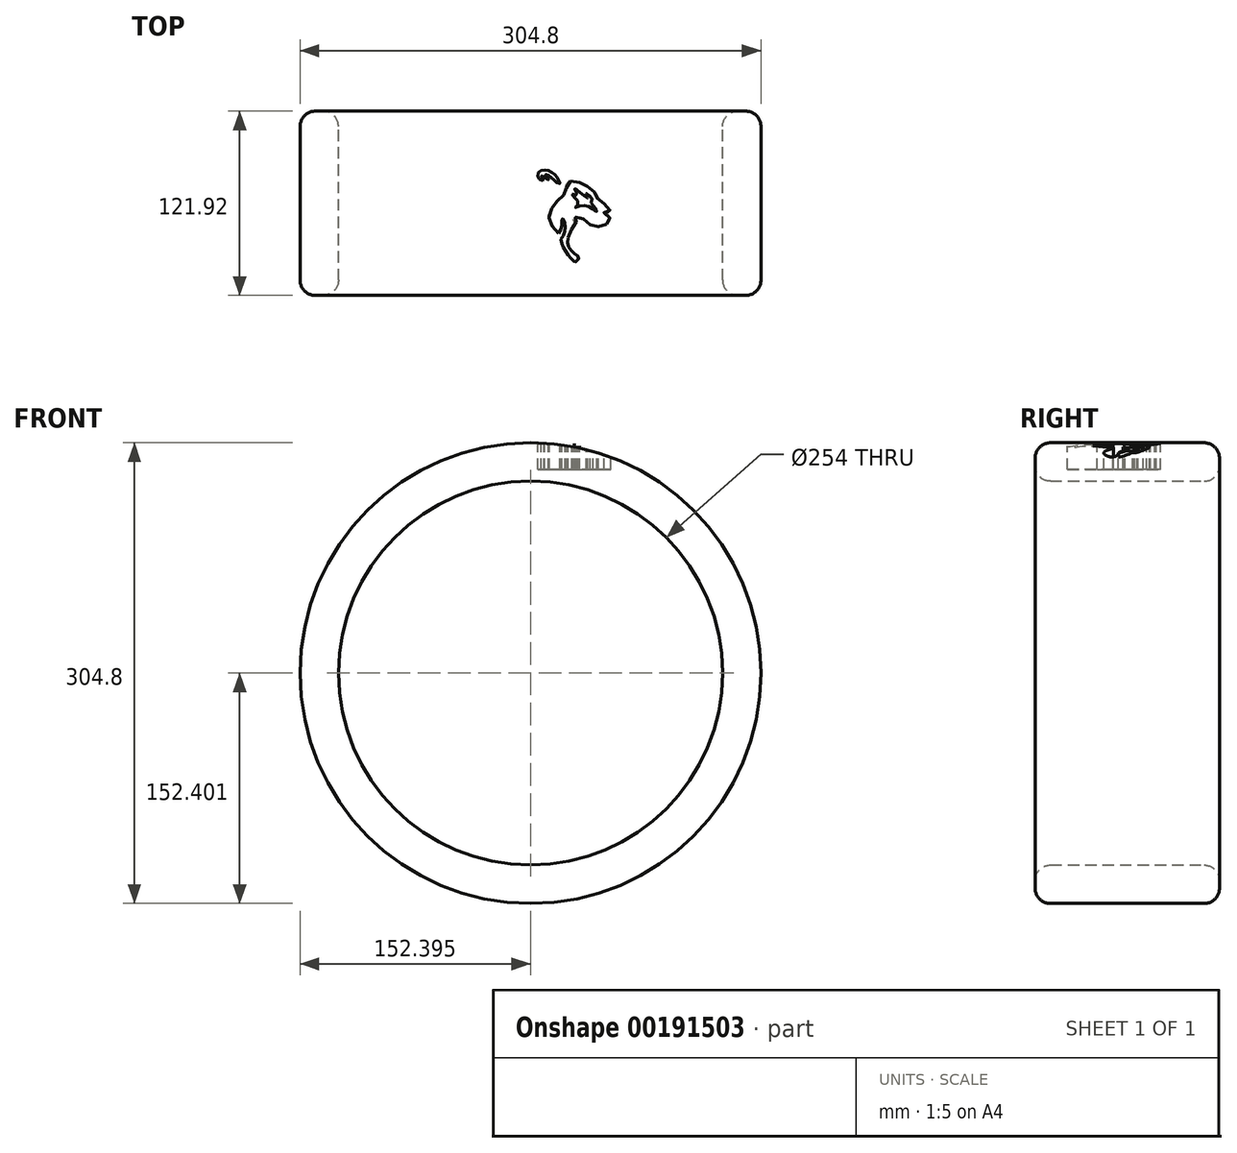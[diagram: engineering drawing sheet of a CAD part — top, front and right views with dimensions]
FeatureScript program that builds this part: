
annotation { "Feature Type Name" : "Feature", "Feature Type Description" : "" }
export const myFeature = defineFeature(function(context is Context, id is Id, definition is map)
    precondition{}
    {
        {
            var Q0;
            Q0=qCreatedBy(makeId("Top.planeOp"),FACE);
            var sketch = newSketch(context, id + "F0", { "sketchPlane" : qUnion([Q0])});
            skFitSpline(sketch, "E0", {"points": [v(-14.87, -19.96) * mm, v(-16.53, -17.13) * mm, v(-18.86, -13.58) * mm, v(-21.78, -9.61) * mm, v(-24.55, -6.73) * mm, v(-29.24, -2.2) * mm, v(-33.32, 1.06) * mm, v(-37.46, 3.8) * mm, v(-40.9, 5.46) * mm, v(-43.35, 6.3) * mm, v(-45.8, 6.8) * mm, v(-46.1, 7) * mm, v(-45.1, 7.59) * mm, v(-39.68, 8.6) * mm, v(-34.05, 9.1) * mm, v(-26.3, 9.07) * mm, v(-20, 8.52) * mm, v(-11.98, 6.95) * mm, v(-2.95, 4.5) * mm, v(7.46, -0.37) * mm, v(7.58, -0.43) * mm, v(5.39, 1.58) * mm, v(1.22, 4.64) * mm, v(-6.3, 8.72) * mm, v(-13.47, 10.97) * mm, v(-20.35, 12.54) * mm, v(-32.07, 13.18) * mm, v(-42.1, 12.72) * mm, v(-42, 12.83) * mm, v(-37.72, 17.5) * mm, v(-31.7, 23.1) * mm, v(-29.15, 25.2) * mm, v(-24.9, 25.08) * mm, v(-20.47, 24.47) * mm, v(-15.32, 23.36) * mm, v(-11.1, 22.1) * mm, v(-6, 20.24) * mm, v(-1.72, 18.52) * mm, v(2.27, 16.6) * mm, v(8.16, 13.3) * mm, v(13.4, 9.63) * mm, v(15.68, 7.8) * mm, v(15.68, 7.82) * mm, v(14.13, 9.77) * mm, v(12.1, 12.08) * mm, v(8.3, 15.63) * mm, v(5.1, 18.14) * mm, v(0.78, 20.85) * mm, v(-6.8, 24.67) * mm, v(-16.6, 27.67) * mm, v(-19.8, 28.49) * mm, v(-23.88, 28.93) * mm, v(-27.84, 29.13) * mm, v(-28.83, 29.25) * mm, v(-28.25, 30.03) * mm, v(-24.92, 31.85) * mm, v(-18.83, 34.06) * mm, v(-13.56, 35.28) * mm, v(-9.07, 35.69) * mm, v(-3.03, 35.3) * mm, v(3.32, 33.44) * mm, v(8.22, 31.43) * mm, v(14.57, 27.73) * mm, v(19.8, 23.97) * mm, v(25.5, 18.58) * mm, v(29.06, 15.28) * mm, v(29.06, 15.31) * mm, v(27.98, 16.94) * mm, v(25.97, 19.45) * mm, v(22.94, 23.1) * mm, v(19.59, 26.07) * mm, v(16.79, 28.66) * mm, v(12.12, 32.04) * mm, v(7.7, 34.26) * mm, v(0, 37.44) * mm, v(-4.46, 38.57) * mm, v(-9.33, 39.6) * mm, v(-9.3, 39.74) * mm, v(-7.35, 40.32) * mm, v(1.8, 40.56) * mm, v(8.65, 39.94) * mm, v(15.65, 38.31) * mm, v(20.75, 36.65) * mm, v(27.72, 32.86) * mm, v(27.72, 32.89) * mm, v(27.46, 36.7) * mm, v(27.52, 36.77) * mm, v(31.83, 34.93) * mm, v(36.67, 32.57) * mm, v(42.64, 28.75) * mm, v(48.48, 24.06) * mm, v(52.7, 18.98) * mm, v(54.89, 13.8) * mm, v(55.33, 9.69) * mm, v(55.18, 7.18) * mm, v(55.27, 7.1) * mm, v(57.42, 4.85) * mm, v(60.51, 1.35) * mm, v(61.91, -0.72) * mm, v(61.88, -0.8) * mm, v(60.78, -1.71) * mm, v(60.9, -1.8) * mm, v(63.2, -4.3) * mm, v(66.14, -7.78) * mm, v(67.85, -11.11) * mm, v(67.85, -13.12) * mm, v(67.46, -14.96) * mm, v(65.54, -18.66) * mm, v(63.46, -20.9) * mm, v(62.06, -22.18) * mm, v(62.03, -22.43) * mm, v(60.9, -24.65) * mm, v(58.62, -26.9) * mm, v(55.24, -28.88) * mm, v(52.93, -29.11) * mm, v(52.9, -28.97) * mm, v(54.07, -26.96) * mm, v(53.95, -27.07) * mm, v(52.2, -28.1) * mm, v(50.31, -28.74) * mm, v(46.46, -28.82) * mm, v(46.5, -28.65) * mm, v(49.67, -22.96) * mm, v(49.32, -22.67) * mm, v(48.18, -21.97) * mm, v(47.13, -20.96) * mm, v(47.05, -20.96) * mm, v(46.7, -21.42) * mm, v(45.15, -23.14) * mm, v(44.22, -23.85) * mm, v(44.1, -24.19) * mm, v(44.19, -29.7) * mm, v(44.22, -29.7) * mm, v(44.92, -28.76) * mm, v(44.95, -28.8) * mm, v(45.44, -29.35) * mm, v(45.8, -30.37) * mm, v(45.9, -32.23) * mm, v(46, -32.23) * mm, v(47.48, -30.69) * mm, v(47.54, -30.69) * mm, v(47.98, -31.21) * mm, v(48.42, -32.87) * mm, v(48.68, -36.43) * mm, v(47.54, -38.62) * mm, v(47.37, -39.43) * mm, v(46.46, -42.26) * mm, v(44.66, -45.2) * mm, v(41.97, -47.1) * mm, v(38.65, -48.03) * mm, v(34.77, -47.92) * mm, v(34.74, -47.86) * mm, v(36.17, -45.32) * mm, v(36.17, -45.26) * mm, v(34.07, -43.66) * mm, v(30.98, -41.07) * mm, v(29.12, -39.32) * mm, v(27.14, -36.66) * mm, v(26.2, -34.83) * mm, v(25.45, -32.87) * mm, v(24.9, -30.05) * mm, v(24.75, -28.85) * mm, v(24.66, -28.8) * mm, v(23.29, -27.54) * mm, v(21.74, -25.69) * mm, v(20.52, -23.85) * mm, v(18.68, -20.22) * mm, v(17.37, -17.45) * mm, v(16.55, -14.63) * mm, v(15.91, -12.2) * mm, v(15.77, -9.76) * mm, v(15.68, -9.76) * mm, v(15.36, -12.64) * mm, v(15.27, -16.23) * mm, v(16.12, -20.1) * mm, v(17.46, -23.43) * mm, v(19.24, -26.14) * mm, v(22.06, -29.32) * mm, v(22.27, -29.52) * mm, v(22.3, -30.95) * mm, v(22.73, -33.22) * mm, v(23.96, -35.85) * mm, v(23.93, -36) * mm, v(22.82, -36.98) * mm, v(20.93, -39.55) * mm, v(19.88, -41.24) * mm, v(19.24, -43.28) * mm, v(19.1, -43.4) * mm, v(18.57, -43.08) * mm, v(17.87, -42.17) * mm, v(17.08, -41.15) * mm, v(16.06, -39.6) * mm, v(15.65, -38.9) * mm, v(15.62, -38.94) * mm, v(14.51, -40.3) * mm, v(13.32, -42.03) * mm, v(11.95, -44.27) * mm, v(11.07, -46.34) * mm, v(10.35, -48.41) * mm, v(9.62, -50.86) * mm, v(9.35, -52.58) * mm, v(9.3, -52.58) * mm, v(7.52, -52.23) * mm, v(6.06, -51.74) * mm, v(4.14, -50.95) * mm, v(2.62, -50.28) * mm, v(0.46, -49.2) * mm, v(-0.88, -48.32) * mm, v(-2.69, -47.13) * mm, v(-4.06, -46.14) * mm, v(-5.37, -45) * mm, v(-6.5, -43.86) * mm, v(-7.09, -43.08) * mm, v(-7.35, -41.82) * mm, v(-7.58, -39.96) * mm, v(-8.43, -37.07) * mm, v(-9.27, -34.13) * mm, v(-10.79, -29.55) * mm, v(-12.22, -25.9) * mm, v(-14.26, -21.53) * mm, v(-14.87, -19.96) * mm]});
            skFitSpline(sketch, "E1", {"points": [v(20.64, 14.12) * mm, v(21.76, 13.88) * mm, v(23.17, 13.2) * mm, v(24.26, 12.5) * mm, v(25.27, 11.74) * mm, v(26.44, 10.52) * mm, v(27.07, 9.84) * mm, v(27.64, 9.1) * mm, v(27.7, 9.06) * mm, v(30.4, 7.75) * mm, v(30.5, 7.73) * mm, v(30.46, 7.97) * mm, v(30.13, 9) * mm, v(29.51, 10.69) * mm, v(28.86, 12.03) * mm, v(27.76, 13.35) * mm, v(26.8, 14.2) * mm, v(25.54, 15.12) * mm, v(24.24, 15.9) * mm, v(23, 16.5) * mm, v(21.47, 16.84) * mm, v(19.08, 16.75) * mm, v(17.8, 16.44) * mm, v(16.92, 15.9) * mm, v(16.42, 15.22) * mm, v(16.11, 14.43) * mm, v(15.98, 12.98) * mm, v(16.3, 11.89) * mm, v(16.76, 11.13) * mm, v(17.4, 10.34) * mm, v(17.5, 10.21) * mm, v(20.2, 10.12) * mm, v(20.2, 10.16) * mm, v(20, 10.47) * mm, v(19.46, 11.3) * mm, v(18.95, 11.9) * mm, v(18.42, 12.67) * mm, v(18.18, 13.08) * mm, v(18.18, 13.1) * mm, v(18.77, 12.97) * mm, v(20.42, 12.07) * mm, v(21.6, 11.22) * mm, v(23.34, 10) * mm, v(23.4, 10.01) * mm, v(23.45, 10.34) * mm, v(22.77, 11.31) * mm, v(21.82, 12.43) * mm, v(21.06, 13.19) * mm, v(20.47, 13.8) * mm, v(20.36, 14.07) * mm, v(20.64, 14.12) * mm]});
            skFitSpline(sketch, "E2", {"points": [v(29.5, -24.96) * mm, v(28.58, -24.35) * mm, v(27.6, -23.28) * mm, v(26.55, -21.99) * mm, v(25.54, -20.52) * mm, v(24.7, -18.86) * mm, v(23.88, -16.81) * mm, v(23.47, -15.09) * mm, v(22.99, -12.75) * mm, v(23.1, -12.53) * mm, v(23.95, -10.91) * mm, v(24.86, -9.04) * mm, v(25.75, -7.35) * mm, v(26.7, -5.8) * mm, v(27.88, -4.41) * mm, v(29.43, -2.66) * mm, v(31.27, -0.9) * mm, v(33.27, 0.81) * mm, v(35.98, 3.21) * mm, v(35.98, 3.28) * mm, v(35.63, 3.76) * mm, v(35.07, 4.35) * mm, v(34.8, 4.96) * mm, v(34.63, 5.81) * mm, v(34.7, 7.06) * mm, v(34.93, 7.73) * mm, v(35.94, 8.78) * mm, v(36.81, 9.33) * mm, v(38.01, 9.61) * mm, v(39.35, 9.66) * mm, v(40.85, 9.42) * mm, v(42.3, 9.1) * mm, v(43.98, 8.55) * mm, v(45.84, 7.68) * mm, v(47.83, 6.54) * mm, v(49.9, 5.2) * mm, v(51.6, 3.98) * mm, v(52.98, 2.8) * mm, v(53.93, 1.93) * mm, v(55, 0.77) * mm, v(56.05, -0.54) * mm, v(56.03, -0.56) * mm, v(54.91, -1.2) * mm, v(56.03, -2.2) * mm, v(57.65, -3.42) * mm, v(59.34, -4.88) * mm, v(61.47, -7.1) * mm, v(63.04, -8.9) * mm, v(64.22, -10.48) * mm, v(64.2, -10.5) * mm, v(59.74, -11.02) * mm, v(59.72, -11.02) * mm, v(59.74, -11.42) * mm, v(59.9, -11.48) * mm, v(60.57, -11.75) * mm, v(62.04, -12.36) * mm, v(62.65, -12.6) * mm, v(62.67, -12.62) * mm, v(62.71, -13.34) * mm, v(62.89, -13.71) * mm, v(63.48, -14.6) * mm, v(64.22, -15.52) * mm, v(64.24, -15.74) * mm, v(63.94, -16.3) * mm, v(63.43, -17) * mm, v(62.73, -17.9) * mm, v(61.93, -18.67) * mm, v(60.8, -19.43) * mm, v(59.6, -19.98) * mm, v(58.43, -20.37) * mm, v(57.17, -20.61) * mm, v(54.26, -20.46) * mm, v(52.54, -20.04) * mm, v(51.49, -19.56) * mm, v(49.87, -18.62) * mm, v(48.5, -17.51) * mm, v(47.3, -16.44) * mm, v(45.88, -15.17) * mm, v(44.76, -14.52) * mm, v(44.04, -14.3) * mm, v(41.64, -14.17) * mm, v(40.04, -14.54) * mm, v(39.04, -15.41) * mm, v(39.08, -15.44) * mm, v(41.8, -16.57) * mm, v(41.82, -16.65) * mm, v(40.93, -18) * mm, v(39.82, -19.8) * mm, v(38.1, -22.76) * mm, v(36.88, -24.94) * mm, v(36.12, -27.16) * mm, v(35.87, -29.14) * mm, v(35.87, -32.06) * mm, v(36.24, -33.32) * mm, v(37, -35.08) * mm, v(38.26, -36.67) * mm, v(39.49, -37.84) * mm, v(41.2, -39.1) * mm, v(42.76, -39.92) * mm, v(43.55, -40.27) * mm, v(43.61, -40.33) * mm, v(43.34, -41.19) * mm, v(42.78, -42.37) * mm, v(41.7, -43.5) * mm, v(39.96, -44.59) * mm, v(39.96, -44.57) * mm, v(40.25, -43.87) * mm, v(40.3, -43.77) * mm, v(39.86, -43.27) * mm, v(38.83, -42.37) * mm, v(37.58, -41.13) * mm, v(36.04, -39.4) * mm, v(34.86, -37.76) * mm, v(33.78, -36.12) * mm, v(32.58, -33.71) * mm, v(31.7, -31.43) * mm, v(31.06, -29.18) * mm, v(31.06, -29.1) * mm, v(31.73, -28.48) * mm, v(32.62, -26.8) * mm, v(33.3, -25.15) * mm, v(33.67, -23.64) * mm, v(33.9, -21.67) * mm, v(33.87, -19.43) * mm, v(33.67, -17.84) * mm, v(33.1, -16.36) * mm, v(31.92, -14.6) * mm, v(31.92, -14.67) * mm, v(31.88, -16.13) * mm, v(31.92, -18.77) * mm, v(31.78, -19.78) * mm, v(31.5, -21.26) * mm, v(31.1, -22.48) * mm, v(30.62, -23.69) * mm, v(29.88, -24.82) * mm, v(29.5, -24.96) * mm]});
            skFitSpline(sketch, "E3", {"points": [v(38.42, 1.18) * mm, v(39.29, 1.15) * mm, v(40.25, 0.8) * mm, v(41.21, 0.31) * mm, v(41.88, -0.27) * mm, v(42, 1.04) * mm, v(41.85, 1.4) * mm, v(41.47, 2.15) * mm, v(40.8, 3.44) * mm, v(40.14, 5.4) * mm, v(40.27, 5.48) * mm, v(40.92, 4.71) * mm, v(42.09, 3.55) * mm, v(43.78, 2.2) * mm, v(45.64, 0.72) * mm, v(48.76, -1.62) * mm, v(48.65, -0.59) * mm, v(48.35, 0.81) * mm, v(48.14, 1.88) * mm, v(48.27, 1.95) * mm, v(49.02, 1.25) * mm, v(50, 0.31) * mm, v(51.08, -1) * mm, v(52.33, -3.64) * mm, v(51.05, -4.61) * mm, v(50.7, -5.43) * mm, v(52.05, -6.37) * mm, v(54, -8.43) * mm, v(55.42, -10.4) * mm, v(55.36, -10.94) * mm, v(54.7, -10.56) * mm, v(53.66, -9.71) * mm, v(52.53, -8.9) * mm, v(51.42, -8.2) * mm, v(50.02, -7.38) * mm, v(48.75, -6.77) * mm, v(48.26, -6.65) * mm, v(47.4, -6.6) * mm, v(46.02, -6.65) * mm, v(44.24, -6.89) * mm, v(42.3, -7.38) * mm, v(40.41, -7.78) * mm, v(40.83, -6.76) * mm, v(42.29, -6.14) * mm, v(42.68, -5.5) * mm, v(42.64, -4.48) * mm, v(42.09, -3.21) * mm, v(40.68, -1.57) * mm, v(39.33, -0.38) * mm, v(38.62, 0.45) * mm, v(38.42, 0.86) * mm, v(38.42, 1.18) * mm]});
            skFitSpline(sketch, "E4.0", {"points": [v(-37, 28.67) * mm, v(-36.89, 28.92) * mm, v(-36.76, 29.16) * mm, v(-36.57, 29.48) * mm, v(-36.3, 29.86) * mm, v(-35.9, 30.24) * mm, v(-35.52, 30.53) * mm, v(-35.17, 30.74) * mm, v(-34.88, 30.9) * mm, v(-34.64, 31) * mm, v(-34.44, 31.1) * mm, v(-34.26, 31.2) * mm, v(-34.04, 31.32) * mm, v(-33.79, 31.47) * mm, v(-33.42, 31.7) * mm, v(-32.9, 32.04) * mm, v(-32.2, 32.49) * mm, v(-31.46, 32.97) * mm, v(-30.66, 33.45) * mm, v(-29.97, 33.85) * mm, v(-29.4, 34.16) * mm, v(-28.83, 34.46) * mm, v(-28.13, 34.78) * mm, v(-27.05, 35.24) * mm, v(-26.05, 35.64) * mm, v(-25.09, 36.06) * mm, v(-24.38, 36.4) * mm, v(-23.78, 36.72) * mm, v(-23.3, 37.01) * mm, v(-22.8, 37.33) * mm, v(-22.15, 37.79) * mm, v(-21.3, 38.43) * mm, v(-20.43, 39.12) * mm, v(-19.53, 39.85) * mm, v(-18.62, 40.6) * mm, v(-17.7, 41.32) * mm, v(-16.79, 42.02) * mm, v(-16.02, 42.56) * mm, v(-15.4, 42.95) * mm, v(-14.93, 43.23) * mm, v(-14.45, 43.48) * mm, v(-13.78, 43.79) * mm, v(-12.97, 44.06) * mm, v(-12.06, 44.25) * mm, v(-11.23, 44.33) * mm, v(-10.64, 44.35) * mm, v(-10.23, 44.35) * mm, v(-9.95, 44.35) * mm, v(-9.7, 44.36) * mm, v(-9.4, 44.37) * mm, v(-9, 44.4) * mm, v(-8.49, 44.45) * mm, v(-7.94, 44.52) * mm, v(-7.35, 44.6) * mm, v(-6.82, 44.66) * mm, v(-6.38, 44.7) * mm, v(-5.72, 44.77) * mm, v(-4.7, 44.85) * mm, v(-3.3, 44.93) * mm, v(-1.81, 45) * mm, v(-0.24, 45.06) * mm, v(1.39, 45.1) * mm, v(2.74, 45.1) * mm, v(3.8, 45.08) * mm, v(4.82, 45.04) * mm, v(6.04, 44.95) * mm, v(7.23, 44.85) * mm, v(8.19, 44.76) * mm, v(9.17, 44.67) * mm, v(10.2, 44.57) * mm, v(11.21, 44.46) * mm, v(11.95, 44.36) * mm, v(12.54, 44.27) * mm, v(13, 44.18) * mm, v(13.34, 44.1) * mm, v(13.65, 44.03) * mm, v(14.02, 43.93) * mm, v(14.41, 43.81) * mm, v(14.8, 43.7) * mm, v(15.15, 43.62) * mm, v(15.47, 43.57) * mm, v(15.84, 43.52) * mm, v(16.44, 43.45) * mm, v(17.33, 43.4) * mm, v(18.33, 43.35) * mm, v(19.41, 43.3) * mm, v(20.92, 43.25) * mm, v(22.47, 43.18) * mm, v(23.95, 43.07) * mm, v(25, 42.96) * mm, v(26, 42.82) * mm, v(26.89, 42.63) * mm, v(27.7, 42.41) * mm, v(28.43, 42.17) * mm, v(29.1, 41.91) * mm, v(29.64, 41.7) * mm, v(30.05, 41.52) * mm, v(30.46, 41.35) * mm, v(31, 41.13) * mm, v(31.7, 40.85) * mm, v(32.67, 40.45) * mm, v(33.69, 40.03) * mm, v(34.7, 39.6) * mm, v(35.45, 39.26) * mm, v(36.17, 38.92) * mm, v(37.09, 38.47) * mm, v(38.15, 37.91) * mm, v(39.13, 37.39) * mm, v(39.87, 36.99) * mm, v(40.6, 36.6) * mm, v(41.53, 36.1) * mm, v(42.66, 35.5) * mm, v(43.81, 34.85) * mm, v(44.77, 34.25) * mm, v(45.54, 33.75) * mm, v(46.1, 33.36) * mm, v(46.66, 32.94) * mm, v(47.18, 32.54) * mm, v(47.67, 32.14) * mm, v(48.15, 31.75) * mm, v(48.62, 31.37) * mm, v(49, 31.07) * mm, v(49.31, 30.84) * mm, v(49.64, 30.6) * mm, v(50.06, 30.29) * mm, v(50.6, 29.88) * mm, v(51.17, 29.45) * mm, v(51.65, 29.05) * mm, v(52.04, 28.7) * mm, v(52.33, 28.42) * mm, v(52.61, 28.13) * mm, v(52.97, 27.75) * mm, v(53.38, 27.27) * mm, v(53.83, 26.7) * mm, v(54.25, 26.15) * mm, v(54.63, 25.65) * mm, v(54.93, 25.26) * mm, v(55.15, 24.99) * mm, v(55.38, 24.71) * mm, v(55.68, 24.37) * mm, v(56.05, 23.94) * mm, v(56.44, 23.49) * mm, v(56.83, 23) * mm, v(57.23, 22.46) * mm, v(57.6, 21.9) * mm, v(58.06, 21.15) * mm, v(58.57, 20.18) * mm, v(59.13, 18.98) * mm, v(59.62, 17.76) * mm, v(59.98, 16.77) * mm, v(60.23, 16.02) * mm, v(60.45, 15.29) * mm, v(60.7, 14.37) * mm, v(61.06, 13.09) * mm, v(61.53, 11.43) * mm, v(62, 9.95) * mm, v(62.37, 8.83) * mm, v(62.65, 8.05) * mm, v(62.88, 7.5) * mm, v(63.05, 7.13) * mm, v(63.16, 6.9) * mm, v(63.26, 6.73) * mm, v(63.38, 6.53) * mm, v(63.52, 6.34) * mm, v(63.72, 6.1) * mm, v(63.96, 5.84) * mm, v(64.2, 5.58) * mm, v(64.46, 5.28) * mm, v(64.79, 4.88) * mm, v(65.19, 4.37) * mm, v(65.59, 3.84) * mm, v(65.99, 3.28) * mm, v(66.39, 2.7) * mm, v(66.78, 2.12) * mm, v(67.16, 1.55) * mm, v(67.51, 1) * mm, v(67.84, 0.49) * mm, v(68.11, 0.03) * mm, v(68.34, -0.36) * mm, v(68.51, -0.67) * mm, v(68.65, -0.92) * mm, v(68.8, -1.2) * mm, v(69.07, -1.66) * mm, v(69.4, -2.22) * mm, v(69.79, -2.85) * mm, v(70.2, -3.51) * mm, v(70.61, -4.17) * mm, v(71.01, -4.79) * mm, v(71.37, -5.32) * mm, v(71.68, -5.77) * mm, v(71.97, -6.16) * mm, v(72.24, -6.53) * mm, v(72.54, -6.9) * mm, v(72.85, -7.3) * mm, v(73.24, -7.8) * mm, v(73.65, -8.36) * mm, v(74.06, -9.02) * mm, v(74.38, -9.66) * mm, v(74.6, -10.22) * mm, v(74.72, -10.6) * mm, v(74.8, -10.92) * mm, v(74.87, -11.22) * mm, v(74.92, -11.6) * mm, v(74.96, -12.03) * mm, v(74.99, -12.59) * mm, v(74.97, -13.24) * mm, v(74.9, -13.92) * mm, v(74.84, -14.4) * mm, v(74.79, -14.72) * mm, v(74.74, -15.02) * mm, v(74.67, -15.4) * mm, v(74.58, -15.8) * mm, v(74.48, -16.12) * mm, v(74.36, -16.45) * mm, v(74.21, -16.83) * mm, v(74.03, -17.26) * mm, v(73.87, -17.61) * mm, v(73.76, -17.88) * mm, v(73.64, -18.15) * mm, v(73.49, -18.53) * mm, v(73.27, -19.04) * mm, v(73.06, -19.5) * mm, v(72.85, -19.88) * mm, v(72.68, -20.17) * mm, v(72.48, -20.47) * mm, v(72.28, -20.73) * mm, v(72.09, -20.97) * mm, v(71.85, -21.24) * mm, v(71.63, -21.47) * mm, v(71.47, -21.65) * mm, v(71.38, -21.75) * mm, v(71.33, -21.81) * mm, v(71.27, -21.88) * mm, v(71.2, -21.98) * mm, v(71.09, -22.1) * mm, v(70.94, -22.3) * mm, v(70.76, -22.54) * mm, v(70.54, -22.8) * mm, v(70.36, -23.02) * mm, v(70.17, -23.22) * mm, v(69.93, -23.47) * mm, v(69.62, -23.76) * mm, v(69.34, -24.02) * mm, v(69.13, -24.22) * mm, v(68.99, -24.35) * mm, v(68.84, -24.5) * mm, v(68.64, -24.68) * mm, v(68.37, -24.94) * mm, v(68.06, -25.21) * mm, v(67.8, -25.44) * mm, v(67.5, -25.67) * mm, v(67.18, -25.9) * mm, v(66.91, -26.11) * mm, v(66.75, -26.24) * mm, v(66.66, -26.32) * mm, v(66.6, -26.37) * mm, v(66.6, -26.38) * mm, v(66.59, -26.4) * mm, v(66.56, -26.44) * mm, v(66.5, -26.52) * mm, v(66.43, -26.64) * mm, v(66.33, -26.82) * mm, v(66.22, -27) * mm, v(66.1, -27.15) * mm, v(66, -27.3) * mm, v(65.88, -27.49) * mm, v(65.72, -27.7) * mm, v(65.52, -27.95) * mm, v(65.28, -28.26) * mm, v(65.06, -28.54) * mm, v(64.92, -28.73) * mm, v(64.81, -28.9) * mm, v(64.7, -29.07) * mm, v(64.52, -29.32) * mm, v(64.27, -29.68) * mm, v(63.97, -30.05) * mm, v(63.74, -30.3) * mm, v(63.58, -30.47) * mm, v(63.37, -30.67) * mm, v(63.12, -30.89) * mm, v(62.78, -31.15) * mm, v(62.38, -31.44) * mm, v(61.98, -31.7) * mm, v(61.68, -31.89) * mm, v(61.47, -32.02) * mm, v(61.25, -32.16) * mm, v(60.94, -32.35) * mm, v(60.52, -32.6) * mm, v(60.06, -32.85) * mm, v(59.67, -33.04) * mm, v(59.35, -33.18) * mm, v(59.08, -33.28) * mm, v(58.85, -33.36) * mm, v(58.63, -33.43) * mm, v(58.38, -33.5) * mm, v(58.02, -33.6) * mm, v(57.65, -33.69) * mm, v(57.3, -33.79) * mm, v(57.06, -33.89) * mm, v(56.87, -33.99) * mm, v(56.7, -34.08) * mm, v(56.52, -34.21) * mm, v(56.24, -34.41) * mm, v(55.88, -34.72) * mm, v(55.45, -35.15) * mm, v(55.06, -35.61) * mm, v(54.74, -36.06) * mm, v(54.55, -36.4) * mm, v(54.46, -36.62) * mm, v(54.38, -36.84) * mm, v(54.3, -37.13) * mm, v(54.24, -37.55) * mm, v(54.2, -37.99) * mm, v(54.16, -38.39) * mm, v(54.13, -38.71) * mm, v(54.1, -39.01) * mm, v(54.05, -39.26) * mm, v(54, -39.52) * mm, v(53.93, -39.84) * mm, v(53.8, -40.32) * mm, v(53.62, -40.89) * mm, v(53.38, -41.51) * mm, v(53.14, -42.1) * mm, v(52.96, -42.55) * mm, v(52.82, -42.9) * mm, v(52.69, -43.27) * mm, v(52.51, -43.77) * mm, v(52.28, -44.43) * mm, v(52.02, -45.13) * mm, v(51.7, -45.87) * mm, v(51.38, -46.5) * mm, v(51.08, -47.02) * mm, v(50.75, -47.53) * mm, v(50.3, -48.12) * mm, v(49.7, -48.78) * mm, v(48.85, -49.58) * mm, v(47.72, -50.46) * mm, v(46.3, -51.35) * mm, v(44.83, -52.1) * mm, v(43.35, -52.7) * mm, v(41.9, -53.15) * mm, v(40.51, -53.43) * mm, v(39.39, -53.55) * mm, v(38.61, -53.58) * mm, v(38.17, -53.59) * mm, v(37.71, -53.6) * mm, v(37.13, -53.58) * mm, v(36.41, -53.53) * mm, v(35.8, -53.45) * mm, v(35.3, -53.36) * mm, v(34.93, -53.27) * mm, v(34.62, -53.18) * mm, v(34.36, -53.1) * mm, v(34.13, -53) * mm, v(33.87, -52.9) * mm, v(33.52, -52.74) * mm, v(33.22, -52.6) * mm, v(32.99, -52.53) * mm, v(32.78, -52.5) * mm, v(32.53, -52.48) * mm, v(32.3, -52.48) * mm, v(31.98, -52.5) * mm, v(31.58, -52.56) * mm, v(31.1, -52.65) * mm, v(30.4, -52.8) * mm, v(29.38, -53.06) * mm, v(27.54, -53.58) * mm, v(24.94, -54.4) * mm, v(21.58, -55.49) * mm, v(18.76, -56.35) * mm, v(16.6, -56.93) * mm, v(15.03, -57.29) * mm, v(13.78, -57.52) * mm, v(12.83, -57.64) * mm, v(12.13, -57.7) * mm, v(11.45, -57.72) * mm, v(10.6, -57.69) * mm, v(9.63, -57.57) * mm, v(8.63, -57.32) * mm, v(7.95, -57.08) * mm, v(7.5, -56.88) * mm, v(7.2, -56.75) * mm, v(6.97, -56.63) * mm, v(6.82, -56.56) * mm, v(6.75, -56.53) * mm, v(6.72, -56.51) * mm, v(6.7, -56.5) * mm, v(6.69, -56.5) * mm, v(6.67, -56.5) * mm, v(6.57, -56.47) * mm, v(6.33, -56.41) * mm, v(6.03, -56.32) * mm, v(5.83, -56.26) * mm, v(5.64, -56.2) * mm, v(5.38, -56.1) * mm, v(4.96, -55.95) * mm, v(4.4, -55.74) * mm, v(3.72, -55.47) * mm, v(3.18, -55.27) * mm, v(2.78, -55.12) * mm, v(2.52, -55.03) * mm, v(2.33, -54.97) * mm, v(2.21, -54.94) * mm, v(2.11, -54.91) * mm, v(2, -54.88) * mm, v(1.87, -54.86) * mm, v(1.7, -54.82) * mm, v(1.49, -54.78) * mm, v(1.22, -54.72) * mm, v(0.95, -54.64) * mm, v(0.72, -54.55) * mm, v(0.5, -54.46) * mm, v(0.27, -54.34) * mm, v(0.01, -54.2) * mm, v(-0.3, -54.01) * mm, v(-0.65, -53.79) * mm, v(-0.96, -53.59) * mm, v(-1.17, -53.45) * mm, v(-1.4, -53.32) * mm, v(-1.71, -53.14) * mm, v(-2.12, -52.91) * mm, v(-2.56, -52.66) * mm, v(-3.18, -52.28) * mm, v(-3.75, -51.9) * mm, v(-4.2, -51.58) * mm, v(-4.46, -51.41) * mm, v(-4.64, -51.3) * mm, v(-4.82, -51.17) * mm, v(-5.07, -51) * mm, v(-5.54, -50.69) * mm, v(-6.16, -50.24) * mm, v(-6.85, -49.67) * mm, v(-7.36, -49.21) * mm, v(-7.85, -48.74) * mm, v(-8.32, -48.28) * mm, v(-8.68, -47.9) * mm, v(-8.93, -47.63) * mm, v(-9.1, -47.43) * mm, v(-9.29, -47.22) * mm, v(-9.53, -46.92) * mm, v(-9.83, -46.47) * mm, v(-10.07, -45.96) * mm, v(-10.22, -45.55) * mm, v(-10.35, -45.16) * mm, v(-10.48, -44.67) * mm, v(-10.62, -44.07) * mm, v(-10.75, -43.45) * mm, v(-10.89, -42.83) * mm, v(-11.02, -42.23) * mm, v(-11.22, -41.42) * mm, v(-11.5, -40.38) * mm, v(-11.79, -39.32) * mm, v(-12.03, -38.45) * mm, v(-12.27, -37.6) * mm, v(-12.58, -36.54) * mm, v(-12.97, -35.3) * mm, v(-13.42, -34.11) * mm, v(-13.88, -33.06) * mm, v(-14.24, -32.23) * mm, v(-14.5, -31.62) * mm, v(-14.76, -31.02) * mm, v(-15.06, -30.24) * mm, v(-15.28, -29.59) * mm, v(-15.48, -29) * mm, v(-15.6, -28.64) * mm, v(-15.72, -28.33) * mm, v(-15.85, -28) * mm, v(-16.04, -27.54) * mm, v(-16.3, -26.96) * mm, v(-16.56, -26.36) * mm, v(-16.83, -25.77) * mm, v(-17.1, -25.18) * mm, v(-17.36, -24.64) * mm, v(-17.7, -23.96) * mm, v(-18.1, -23.18) * mm, v(-18.62, -22.23) * mm, v(-19.27, -21.16) * mm, v(-20.03, -20) * mm, v(-20.71, -18.96) * mm, v(-21.28, -18.1) * mm, v(-21.85, -17.25) * mm, v(-22.42, -16.4) * mm, v(-22.98, -15.6) * mm, v(-23.4, -15.03) * mm, v(-23.8, -14.5) * mm, v(-24.31, -13.84) * mm, v(-24.96, -13.07) * mm, v(-25.6, -12.34) * mm, v(-26.06, -11.82) * mm, v(-26.33, -11.5) * mm, v(-26.72, -11.06) * mm, v(-27.29, -10.4) * mm, v(-27.97, -9.64) * mm, v(-28.58, -9) * mm, v(-29.1, -8.5) * mm, v(-29.67, -7.95) * mm, v(-30.47, -7.2) * mm, v(-31.3, -6.46) * mm, v(-32.1, -5.75) * mm, v(-32.65, -5.26) * mm, v(-33.17, -4.8) * mm, v(-33.61, -4.42) * mm, v(-34.01, -4.08) * mm, v(-34.38, -3.78) * mm, v(-34.76, -3.5) * mm, v(-35.18, -3.2) * mm, v(-35.68, -2.89) * mm, v(-36.44, -2.43) * mm, v(-37.54, -1.81) * mm, v(-38.93, -1.06) * mm, v(-40.3, -0.33) * mm, v(-41.29, 0.18) * mm, v(-42, 0.52) * mm, v(-42.5, 0.74) * mm, v(-42.98, 0.92) * mm, v(-43.41, 1.05) * mm, v(-43.93, 1.18) * mm, v(-44.52, 1.32) * mm, v(-45.19, 1.48) * mm, v(-45.93, 1.7) * mm, v(-46.73, 1.99) * mm, v(-47.58, 2.38) * mm, v(-48.41, 2.85) * mm, v(-49.23, 3.41) * mm, v(-49.87, 3.97) * mm, v(-50.34, 4.51) * mm, v(-50.68, 4.98) * mm, v(-50.97, 5.52) * mm, v(-51.16, 6.07) * mm, v(-51.24, 6.57) * mm, v(-51.26, 6.97) * mm, v(-51.24, 7.35) * mm, v(-51.15, 7.84) * mm, v(-50.96, 8.38) * mm, v(-50.68, 8.9) * mm, v(-50.37, 9.34) * mm, v(-49.95, 9.83) * mm, v(-49.42, 10.34) * mm, v(-48.83, 10.86) * mm, v(-48.4, 11.23) * mm, v(-48.13, 11.49) * mm, v(-47.93, 11.68) * mm, v(-47.74, 11.88) * mm, v(-47.5, 12.16) * mm, v(-47.2, 12.51) * mm, v(-46.83, 12.97) * mm, v(-46.45, 13.47) * mm, v(-46.03, 14) * mm, v(-45.43, 14.77) * mm, v(-44.76, 15.54) * mm, v(-44.04, 16.32) * mm, v(-43.46, 16.9) * mm, v(-42.85, 17.47) * mm, v(-42.31, 17.95) * mm, v(-41.87, 18.31) * mm, v(-41.43, 18.66) * mm, v(-40.91, 19.07) * mm, v(-40.34, 19.54) * mm, v(-39.82, 20) * mm, v(-39.38, 20.44) * mm, v(-39, 20.9) * mm, v(-38.74, 21.29) * mm, v(-38.57, 21.63) * mm, v(-38.4, 22) * mm, v(-38.22, 22.56) * mm, v(-38.02, 23.38) * mm, v(-37.86, 24.27) * mm, v(-37.71, 25.21) * mm, v(-37.58, 26.15) * mm, v(-37.46, 26.92) * mm, v(-37.34, 27.52) * mm, v(-37.23, 27.97) * mm, v(-37.11, 28.36) * mm, v(-37, 28.67) * mm, v(-36.89, 28.92) * mm, v(-36.76, 29.16) * mm, v(-37, 28.67) * mm]});
            skSolve(sketch);
        }
        {
            var Q0;
            Q0=makeQuery(id+"F0.imprint","IMPRINT",FACE,{"disambiguationData":[TD([[makeQuery(id+"F0.imprint","IMPRINT",EDGE,{"derivedFrom":sQuery(id+"F0.wireOp",EDGE,"E2")}),-1.0]])]});
            var Q1;
            Q1=makeQuery(id+"F0.imprint","IMPRINT",FACE,{"disambiguationData":[TD([[makeQuery(id+"F0.imprint","IMPRINT",EDGE,{"derivedFrom":sQuery(id+"F0.wireOp",EDGE,"74d6bb4c-ac92-4f57-8e83-752cdc54502e")}),-1.0]])]});
            var Q2;
            Q2=makeQuery(id+"F0.imprint","IMPRINT",FACE,{"disambiguationData":[TD([[makeQuery(id+"F0.imprint","IMPRINT",EDGE,{"derivedFrom":sQuery(id+"F0.wireOp",EDGE,"c6ac5f7b-a27c-41a7-b675-64ae14456e64")}),-1.0]])]});
            var Q3;
            Q3=makeQuery(id+"F0.imprint","IMPRINT",FACE,{"disambiguationData":[TD([[makeQuery(id+"F0.imprint","IMPRINT",EDGE,{"derivedFrom":sQuery(id+"F0.wireOp",EDGE,"E1")}),1.0]])]});
            var Q4;
            Q4=makeQuery(id+"F0.imprint","IMPRINT",FACE,{"disambiguationData":[TD([[makeQuery(id+"F0.imprint","IMPRINT",EDGE,{"derivedFrom":sQuery(id+"F0.wireOp",EDGE,"0e008e9f-14c0-4107-bc9a-aa72c76f3f1f")}),-1.0]])]});
            var Q5;
            Q5=makeQuery(id+"F0.imprint","IMPRINT",FACE,{"disambiguationData":[TD([[makeQuery(id+"F0.imprint","IMPRINT",EDGE,{"derivedFrom":sQuery(id+"F0.wireOp",EDGE,"862c8b35-878f-469a-98d0-ead8ce9435b1")}),-1.0]])]});
            var Q6;
            Q6=makeQuery(id+"F0.imprint","IMPRINT",FACE,{"disambiguationData":[TD([[makeQuery(id+"F0.imprint","IMPRINT",EDGE,{"derivedFrom":sQuery(id+"F0.wireOp",EDGE,"30d3e914-cf87-45c0-9ba4-18f6ca06e4de")}),-1.0]])]});
            var Q7;
            Q7=makeQuery(id+"F0.imprint","IMPRINT",FACE,{"disambiguationData":[TD([[makeQuery(id+"F0.imprint","IMPRINT",EDGE,{"derivedFrom":sQuery(id+"F0.wireOp",EDGE,"2ab885d8-9b60-402b-b28b-6711be7e85d9")}),-1.0]])]});
            var Q8;
            Q8=makeQuery(id+"F0.imprint","IMPRINT",FACE,{"disambiguationData":[TD([[makeQuery(id+"F0.imprint","IMPRINT",EDGE,{"derivedFrom":sQuery(id+"F0.wireOp",EDGE,"69773884-eae4-4e5f-a5ac-bce1ddbc884f")}),-1.0]])]});
            var Q9;
            Q9=makeQuery(id+"F0.imprint","IMPRINT",FACE,{"disambiguationData":[TD([[makeQuery(id+"F0.imprint","IMPRINT",EDGE,{"derivedFrom":sQuery(id+"F0.wireOp",EDGE,"E0")}),1.0]])]});
            extrude(context, id + "F1", {"entities" : qUnion([Q0, Q1, Q2, Q3, Q4, Q5, Q6, Q7, Q8, Q9]), "depth" : 25.4 * mm});
        }
        {
            var Q0;
            Q0=qCreatedBy(makeId("Front.planeOp"),FACE);
            var sketch = newSketch(context, id + "F2", { "sketchPlane" : qUnion([Q0])});
            skLineSegment(sketch, "E5", {"start": v(11.15, 12.65) * mm, "end": v(-46, 12.65) * mm});
            skPoint(sketch, "E6", {"position": v(11.15, 12.65) * mm});
            skSolve(sketch);
        }
        {
            var Q0;
            Q0=qCreatedBy(makeId("Front.planeOp"),FACE);
            cPlane(context, id + "F3", {"entities" : qUnion([Q0]), "cplaneType" : CPlaneType.OFFSET, "offset" : 76.2 * mm, "width" : 152.4 * mm, "height" : 152.4 * mm});
        }
        {
            var Q0;
            Q0=qCreatedBy(id+"F3.planeOp",FACE);
            var sketch = newSketch(context, id + "F4", { "sketchPlane" : qUnion([Q0])});
            skCircle(sketch, "E7", {"center": v(11.15, -139.75) * mm, "radius": 152.4 * mm});
            skSolve(sketch);
        }
        {
            var Q0;
            Q0=makeQuery(id+"F4.imprint","IMPRINT",FACE,{"disambiguationData":[TD([[makeQuery(id+"F4.imprint","IMPRINT",EDGE,{"derivedFrom":sQuery(id+"F4.wireOp",EDGE,"E7")}),1.0]])]});
            extrude(context, id + "F5", {"entities" : qUnion([Q0]), "operationType" : NewBodyOperationType.REMOVE, "oppositeDirection" : true, "depth" : 254 * mm});
        }
        {
            var Q0;
            Q0=qCreatedBy(makeId("Front.planeOp"),FACE);
            cPlane(context, id + "F6", {"entities" : qUnion([Q0]), "cplaneType" : CPlaneType.OFFSET, "offset" : 55.88 * mm, "oppositeDirection" : true, "width" : 152.4 * mm, "height" : 152.4 * mm});
        }
        {
            var Q0;
            Q0=qCreatedBy(id+"F6.planeOp",FACE);
            var sketch = newSketch(context, id + "F7", { "sketchPlane" : qUnion([Q0])});
            skCircle(sketch, "E8", {"center": v(11.15, -139.75) * mm, "radius": 152.4 * mm});
            skCircle(sketch, "E9", {"center": v(11.15, -139.75) * mm, "radius": 127 * mm});
            skSolve(sketch);
        }
        {
            var Q0;
            Q0=makeQuery(id+"F7.imprint","IMPRINT",FACE,{"disambiguationData":[TD([[makeQuery(id+"F7.imprint","IMPRINT",EDGE,{"derivedFrom":sQuery(id+"F7.wireOp",EDGE,"E8")}),1.0]])]});
            extrude(context, id + "F8", {"entities" : qUnion([Q0]), "depth" : 121.92 * mm});
        }
        {
            var Q0;
            Q0=makeQuery(id+"F8.opExtrude","CAP_EDGE",EDGE,{"disambiguationData":[OSD([sQuery(id+"F7.wireOp",EDGE,"E8")])],"isStart":true});
            var Q1;
            Q1=makeQuery(id+"F8.opExtrude","CAP_EDGE",EDGE,{"disambiguationData":[OSD([sQuery(id+"F7.wireOp",EDGE,"E9")])],"isStart":true});
            var Q2;
            Q2=makeQuery(id+"F8.opExtrude","CAP_EDGE",EDGE,{"disambiguationData":[OSD([sQuery(id+"F7.wireOp",EDGE,"E8")])],"isStart":false});
            var Q3;
            Q3=makeQuery(id+"F8.opExtrude","CAP_EDGE",EDGE,{"disambiguationData":[OSD([sQuery(id+"F7.wireOp",EDGE,"E9")])],"isStart":false});
            fillet(context, id + "F9", {"entities" : qUnion([Q0, Q1, Q2, Q3]), "radius" : 10.16 * mm, "tangentPropagation" : true, "allowEdgeOverflow" : false});
        }
        {
            var Q0;
            Q0=makeQuery(id+"F1.opExtrude","CAP_FACE",FACE,{"disambiguationData":[OSD([sQuery(id+"F0.wireOp",EDGE,"74d6bb4c-ac92-4f57-8e83-752cdc54502e"),sQuery(id+"F0.wireOp",EDGE,"E0")])],"isStart":false});
            var Q1;
            Q1=makeQuery(id+"F1.opExtrude","CAP_FACE",FACE,{"disambiguationData":[OSD([sQuery(id+"F0.wireOp",EDGE,"E2"),sQuery(id+"F0.wireOp",EDGE,"E3")])],"isStart":false});
            var Q2;
            Q2=makeQuery(id+"F1.opExtrude","CAP_FACE",FACE,{"disambiguationData":[OSD([sQuery(id+"F0.wireOp",EDGE,"c6ac5f7b-a27c-41a7-b675-64ae14456e64")])],"isStart":false});
            var Q3;
            Q3=makeQuery(id+"F1.opExtrude","CAP_FACE",FACE,{"disambiguationData":[OSD([sQuery(id+"F0.wireOp",EDGE,"862c8b35-878f-469a-98d0-ead8ce9435b1")])],"isStart":false});
            var Q4;
            Q4=makeQuery(id+"F1.opExtrude","CAP_FACE",FACE,{"disambiguationData":[OSD([sQuery(id+"F0.wireOp",EDGE,"0e008e9f-14c0-4107-bc9a-aa72c76f3f1f")])],"isStart":false});
            var Q5;
            Q5=makeQuery(id+"F1.opExtrude","CAP_FACE",FACE,{"disambiguationData":[OSD([sQuery(id+"F0.wireOp",EDGE,"2ab885d8-9b60-402b-b28b-6711be7e85d9")])],"isStart":false});
            var Q6;
            Q6=makeQuery(id+"F1.opExtrude","CAP_FACE",FACE,{"disambiguationData":[OSD([sQuery(id+"F0.wireOp",EDGE,"69773884-eae4-4e5f-a5ac-bce1ddbc884f")])],"isStart":false});
            var Q7;
            Q7=makeQuery(id+"F1.opExtrude","CAP_FACE",FACE,{"disambiguationData":[OSD([sQuery(id+"F0.wireOp",EDGE,"30d3e914-cf87-45c0-9ba4-18f6ca06e4de")])],"isStart":false});
            var Q8;
            Q8=makeQuery(id+"F1.opExtrude","CAP_FACE",FACE,{"disambiguationData":[OSD([sQuery(id+"F0.wireOp",EDGE,"E1")])],"isStart":false});
            extrude(context, id + "F10", {"entities" : qUnion([Q0, Q1, Q2, Q3, Q4, Q5, Q6, Q7, Q8]), "operationType" : NewBodyOperationType.REMOVE, "oppositeDirection" : true, "depth" : 30.48 * mm});
        }
    });
